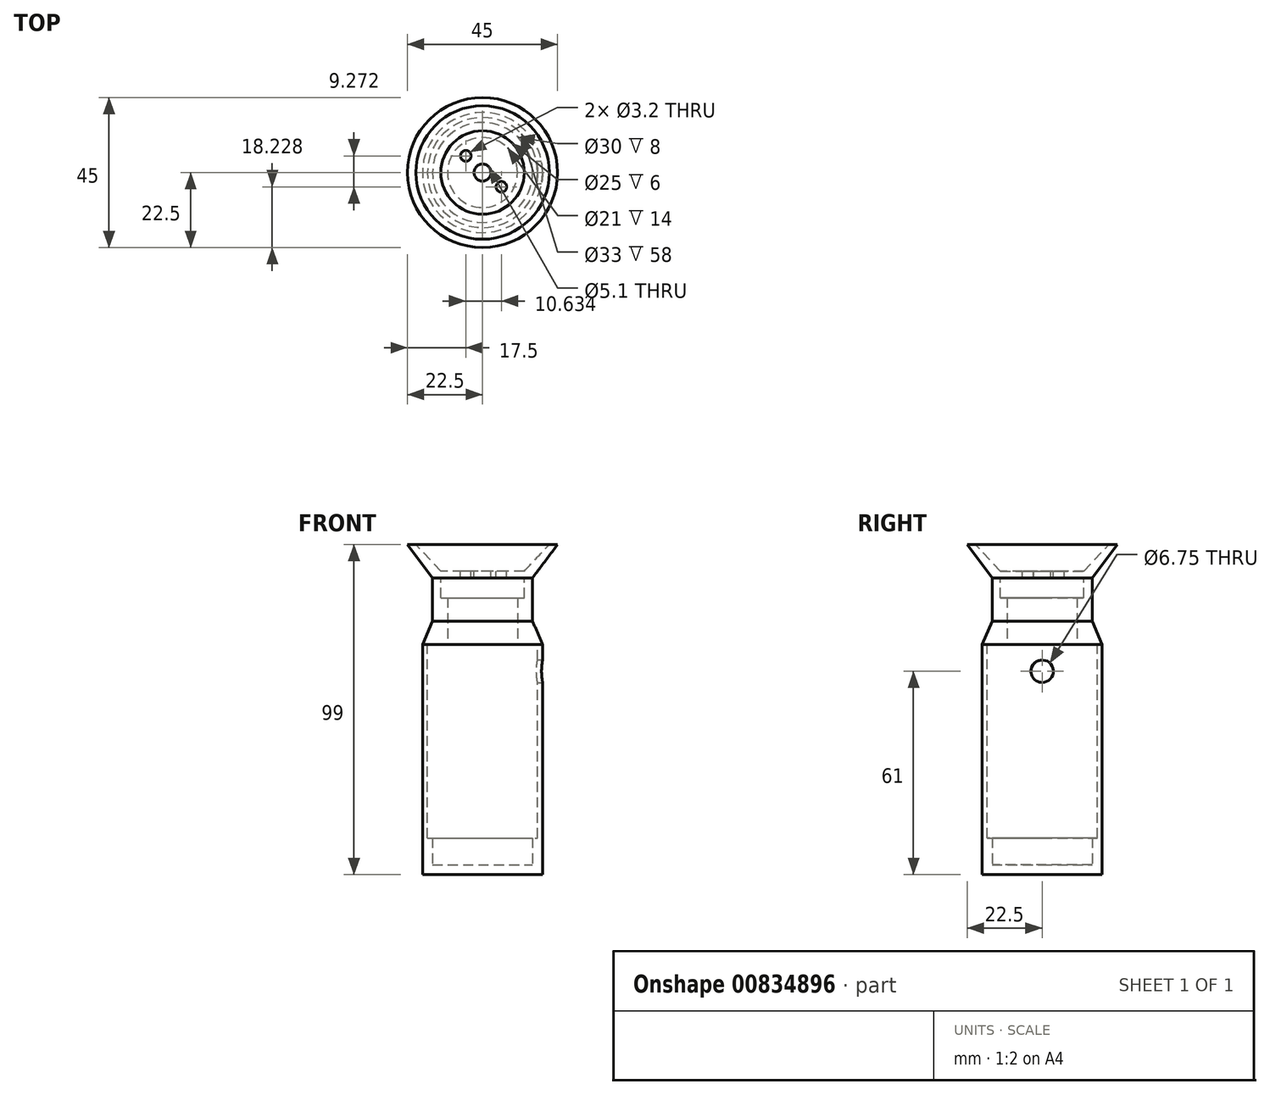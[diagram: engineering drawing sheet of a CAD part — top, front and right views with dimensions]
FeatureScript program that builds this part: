
annotation { "Feature Type Name" : "Feature", "Feature Type Description" : "" }
export const myFeature = defineFeature(function(context is Context, id is Id, definition is map)
    precondition{}
    {
        {
            var Q0;
            Q0=qCreatedBy(makeId("Top.planeOp"),FACE);
            var sketch = newSketch(context, id + "F0", { "sketchPlane" : qUnion([Q0])});
            skCircle(sketch, "E0", {"center": v(0, 0) * mm, "radius": 15 * mm});
            skSolve(sketch);
        }
        {
            var Q0;
            Q0=qCreatedBy(makeId("Top.planeOp"),FACE);
            cPlane(context, id + "F1", {"entities" : qUnion([Q0]), "cplaneType" : CPlaneType.OFFSET, "offset" : 10 * mm, "width" : 150 * mm, "height" : 150 * mm});
        }
        {
            var Q0;
            Q0=qCreatedBy(id+"F1.planeOp",FACE);
            var sketch = newSketch(context, id + "F2", { "sketchPlane" : qUnion([Q0])});
            skCircle(sketch, "E1", {"center": v(0, 0) * mm, "radius": 22.5 * mm});
            skSolve(sketch);
        }
        {
            var Q0;
            Q0 = qSketchRegion(id + "F2", true);
            var Q1;
            Q1 = qSketchRegion(id + "F0", true);
            loft(context, id + "F3", {"sheetProfilesArray" : [{ "sheetProfileEntities" : qUnion([Q0]) }, { "sheetProfileEntities" : qUnion([Q1]) }]});
        }
        {
            var Q0;
            Q0=makeQuery(id+"F3.opLoft","CAP_FACE",FACE,{"disambiguationData":[OSD([makeQuery(id+"F2.imprint","IMPRINT",FACE,{"disambiguationData":[TD([[makeQuery(id+"F2.imprint","IMPRINT",EDGE,{"derivedFrom":sQuery(id+"F2.wireOp",EDGE,"E1")}),1.0]])]})])],"isStart":true});
            var sketch = newSketch(context, id + "F4", { "sketchPlane" : qUnion([Q0])});
            skCircle(sketch, "E2", {"center": v(0, 0) * mm, "radius": 20 * mm});
            skSolve(sketch);
        }
        {
            var Q0;
            Q0=qCreatedBy(makeId("Top.planeOp"),FACE);
            cPlane(context, id + "F5", {"entities" : qUnion([Q0]), "cplaneType" : CPlaneType.OFFSET, "offset" : 2 * mm, "width" : 150 * mm, "height" : 150 * mm});
        }
        {
            var Q0;
            Q0=qCreatedBy(id+"F5.planeOp",FACE);
            var sketch = newSketch(context, id + "F6", { "sketchPlane" : qUnion([Q0])});
            skCircle(sketch, "E3", {"center": v(0, 0) * mm, "radius": 12.5 * mm});
            skSolve(sketch);
        }
        {
            var Q1;
            Q1 = qSketchRegion(id + "F6", true);
            var Q2;
            Q2 = qSketchRegion(id + "F4", true);
            loft(context, id + "F7", {"operationType" : NewBodyOperationType.REMOVE, "sheetProfilesArray" : [{ "sheetProfileEntities" : qUnion([Q1]) }, { "sheetProfileEntities" : qUnion([Q2]) }]});
        }
        {
            var Q0;
            Q0=makeQuery(id+"F3.opLoft","CAP_FACE",FACE,{"disambiguationData":[OSD([makeQuery(id+"F0.imprint","IMPRINT",FACE,{"disambiguationData":[TD([[makeQuery(id+"F0.imprint","IMPRINT",EDGE,{"derivedFrom":sQuery(id+"F0.wireOp",EDGE,"E0")}),1.0]])]})])],"isStart":true});
            var sketch = newSketch(context, id + "F8", { "sketchPlane" : qUnion([Q0])});
            skCircle(sketch, "E4", {"center": v(0, 0) * mm, "radius": 12.5 * mm});
            skSolve(sketch);
        }
        {
            var Q0;
            Q0=makeQuery(id+"F8.imprint","IMPRINT",FACE,{"disambiguationData":[TD([[makeQuery(id+"F8.imprint","IMPRINT",EDGE,{"derivedFrom":sQuery(id+"F8.wireOp",EDGE,"E4")}),-1.0]])]});
            extrude(context, id + "F9", {"entities" : qUnion([Q0]), "operationType" : NewBodyOperationType.ADD, "depth" : 13 * mm, "offsetDistance" : 25 * mm});
        }
        {
            var Q0;
            Q0=makeQuery(id+"F9.opExtrude","CAP_FACE",FACE,{"disambiguationData":[OSD([sQuery(id+"F8.wireOp",EDGE,"E4")])],"isStart":false});
            var sketch = newSketch(context, id + "F10", { "sketchPlane" : qUnion([Q0])});
            skCircle(sketch, "E5", {"center": v(0, 0) * mm, "radius": 10.5 * mm});
            skSolve(sketch);
        }
        {
            var Q0;
            Q0=makeQuery(id+"F10.imprint","IMPRINT",FACE,{"disambiguationData":[TD([[makeQuery(id+"F10.imprint","IMPRINT",EDGE,{"derivedFrom":sQuery(id+"F10.wireOp",EDGE,"E5")}),-1.0]])]});
            extrude(context, id + "F11", {"entities" : qUnion([Q0]), "oppositeDirection" : true, "depth" : 7 * mm, "offsetDistance" : 25 * mm});
        }
        {
            var Q0;
            Q0=makeQuery(id+"F9.opExtrude","CAP_FACE",FACE,{"disambiguationData":[OSD([sQuery(id+"F0.wireOp",EDGE,"E0"),sQuery(id+"F8.wireOp",EDGE,"E4")])],"isStart":false});
            var sketch = newSketch(context, id + "F12", { "sketchPlane" : qUnion([Q0])});
            skCircle(sketch, "E6.0", {"center": v(0, 0) * mm, "radius": 15 * mm});
            skSolve(sketch);
        }
        {
            var Q0;
            Q0=qCreatedBy(makeId("Top.planeOp"),FACE);
            cPlane(context, id + "F13", {"entities" : qUnion([Q0]), "cplaneType" : CPlaneType.OFFSET, "offset" : 20 * mm, "oppositeDirection" : true, "width" : 150 * mm, "height" : 150 * mm});
        }
        {
            var Q0;
            Q0=qCreatedBy(id+"F13.planeOp",FACE);
            var sketch = newSketch(context, id + "F14", { "sketchPlane" : qUnion([Q0])});
            skCircle(sketch, "E7", {"center": v(0, 0) * mm, "radius": 18 * mm});
            skSolve(sketch);
        }
        {
            var Q1;
            Q1 = qSketchRegion(id + "F12", true);
            var Q2;
            Q2 = qSketchRegion(id + "F14", true);
            loft(context, id + "F15", {"operationType" : NewBodyOperationType.ADD, "sheetProfilesArray" : [{ "sheetProfileEntities" : qUnion([Q1]) }, { "sheetProfileEntities" : qUnion([Q2]) }]});
        }
        {
            var Q0;
            Q0=makeQuery(id+"F15.opLoft","CAP_FACE",FACE,{"disambiguationData":[OSD([makeQuery(id+"F14.imprint","IMPRINT",FACE,{"disambiguationData":[TD([[makeQuery(id+"F14.imprint","IMPRINT",EDGE,{"derivedFrom":sQuery(id+"F14.wireOp",EDGE,"E7")}),1.0]])]})])],"isStart":true});
            var sketch = newSketch(context, id + "F16", { "sketchPlane" : qUnion([Q0])});
            skCircle(sketch, "E8", {"center": v(0, 0) * mm, "radius": 10.5 * mm});
            skSolve(sketch);
        }
        {
            var Q0;
            Q0=makeQuery(id+"F16.imprint","IMPRINT",FACE,{"disambiguationData":[TD([[makeQuery(id+"F16.imprint","IMPRINT",EDGE,{"derivedFrom":sQuery(id+"F16.wireOp",EDGE,"E8")}),1.0]])]});
            extrude(context, id + "F17", {"entities" : qUnion([Q0]), "operationType" : NewBodyOperationType.REMOVE, "oppositeDirection" : true, "depth" : 10 * mm, "offsetDistance" : 25 * mm});
        }
        {
            var Q0;
            Q0=makeQuery(id+"F15.opLoft","CAP_FACE",FACE,{"disambiguationData":[OSD([makeQuery(id+"F14.imprint","IMPRINT",FACE,{"disambiguationData":[TD([[makeQuery(id+"F14.imprint","IMPRINT",EDGE,{"derivedFrom":sQuery(id+"F14.wireOp",EDGE,"E7")}),1.0]])]})])],"isStart":true});
            var sketch = newSketch(context, id + "F18", { "sketchPlane" : qUnion([Q0])});
            skCircle(sketch, "E9", {"center": v(0, 0) * mm, "radius": 16.5 * mm});
            skSolve(sketch);
        }
        {
            var Q0;
            Q0=makeQuery(id+"F18.imprint","IMPRINT",FACE,{"disambiguationData":[TD([[makeQuery(id+"F18.imprint","IMPRINT",EDGE,{"derivedFrom":sQuery(id+"F18.wireOp",EDGE,"E9")}),-1.0]])]});
            extrude(context, id + "F19", {"entities" : qUnion([Q0]), "operationType" : NewBodyOperationType.ADD, "depth" : 62 * mm, "offsetDistance" : 25 * mm});
        }
        {
            var Q0;
            Q0=makeQuery(id+"F19.opExtrude","CAP_FACE",FACE,{"disambiguationData":[OSD([sQuery(id+"F14.wireOp",EDGE,"E7"),sQuery(id+"F18.wireOp",EDGE,"E9")])],"isStart":false});
            var sketch = newSketch(context, id + "F20", { "sketchPlane" : qUnion([Q0])});
            skCircle(sketch, "E10", {"center": v(0, 0) * mm, "radius": 15 * mm});
            skSolve(sketch);
        }
        {
            var Q0;
            Q0=makeQuery(id+"F20.imprint","IMPRINT",FACE,{"disambiguationData":[TD([[makeQuery(id+"F20.imprint","IMPRINT",EDGE,{"derivedFrom":sQuery(id+"F20.wireOp",EDGE,"E10")}),-1.0]])]});
            extrude(context, id + "F21", {"entities" : qUnion([Q0]), "oppositeDirection" : true, "depth" : 4 * mm, "offsetDistance" : 25 * mm});
        }
        {
            var Q0;
            Q0=makeQuery(id+"F21.opExtrude","CAP_FACE",FACE,{"disambiguationData":[OSD([sQuery(id+"F18.wireOp",EDGE,"E9"),sQuery(id+"F20.wireOp",EDGE,"E10")])],"isStart":true});
            var Q1;
            Q1=makeQuery(id+"F19.opExtrude","CAP_FACE",FACE,{"disambiguationData":[OSD([sQuery(id+"F14.wireOp",EDGE,"E7"),sQuery(id+"F18.wireOp",EDGE,"E9")])],"isStart":false});
            extrude(context, id + "F22", {"entities" : qUnion([Q0, Q1]), "operationType" : NewBodyOperationType.ADD, "depth" : 4 * mm, "offsetDistance" : 25 * mm});
        }
        {
            var Q0;
            {var subQ0=sQuery(id+"F18.wireOp",EDGE,"E9");Q0=makeQuery(id+"F22.boolean.opBoolean","MERGE",FACE,{"derivedFrom":[makeQuery(id+"F22.opExtrude","CAP_FACE",FACE,{"disambiguationData":[OSD([sQuery(id+"F14.wireOp",EDGE,"E7"),subQ0])],"isStart":false}),makeQuery(id+"F22.opExtrude","CAP_FACE",FACE,{"disambiguationData":[OSD([subQ0,sQuery(id+"F20.wireOp",EDGE,"E10")])],"isStart":false})]});}
            var sketch = newSketch(context, id + "F23", { "sketchPlane" : qUnion([Q0])});
            skCircle(sketch, "E11", {"center": v(0, 0) * mm, "radius": 18 * mm});
            skSolve(sketch);
        }
        {
            var Q0;
            Q0 = qSketchRegion(id + "F23", true);
            extrude(context, id + "F24", {"entities" : qUnion([Q0]), "operationType" : NewBodyOperationType.ADD, "depth" : 3 * mm, "offsetDistance" : 25 * mm});
        }
        {
            var Q0;
            Q0=makeQuery(id+"F7.boolean.opBoolean","COPY",FACE,{"derivedFrom":makeQuery(id+"F7.opLoft","CAP_FACE",FACE,{"disambiguationData":[OSD([makeQuery(id+"F6.imprint","IMPRINT",FACE,{"disambiguationData":[TD([[makeQuery(id+"F6.imprint","IMPRINT",EDGE,{"derivedFrom":sQuery(id+"F6.wireOp",EDGE,"E3")}),1.0]])]})])],"isStart":true})});
            var sketch = newSketch(context, id + "F25", { "sketchPlane" : qUnion([Q0])});
            skCircle(sketch, "E12", {"center": v(0, 0) * mm, "radius": 2.55 * mm});
            skCircle(sketch, "E13", {"center": v(-5, 5) * mm, "radius": 1.6 * mm});
            skCircle(sketch, "E14", {"center": v(5.63, -4.27) * mm, "radius": 1.6 * mm});
            skSolve(sketch);
        }
        {
            var Q0;
            Q0=makeQuery(id+"F25.imprint","IMPRINT",FACE,{"disambiguationData":[TD([[makeQuery(id+"F25.imprint","IMPRINT",EDGE,{"derivedFrom":sQuery(id+"F25.wireOp",EDGE,"E13")}),1.0]])]});
            var Q1;
            Q1=makeQuery(id+"F25.imprint","IMPRINT",FACE,{"disambiguationData":[TD([[makeQuery(id+"F25.imprint","IMPRINT",EDGE,{"derivedFrom":sQuery(id+"F25.wireOp",EDGE,"E12")}),1.0]])]});
            var Q2;
            Q2=makeQuery(id+"F25.imprint","IMPRINT",FACE,{"disambiguationData":[TD([[makeQuery(id+"F25.imprint","IMPRINT",EDGE,{"derivedFrom":sQuery(id+"F25.wireOp",EDGE,"E14")}),1.0]])]});
            extrude(context, id + "F26", {"entities" : qUnion([Q0, Q1, Q2]), "operationType" : NewBodyOperationType.REMOVE, "oppositeDirection" : true, "depth" : 3 * mm, "offsetDistance" : 25 * mm});
        }
        {
            var Q0;
            Q0=qCreatedBy(makeId("Right.planeOp"),FACE);
            cPlane(context, id + "F27", {"entities" : qUnion([Q0]), "cplaneType" : CPlaneType.OFFSET, "offset" : 18 * mm, "width" : 150 * mm, "height" : 150 * mm});
        }
        {
            var Q0;
            Q0=qCreatedBy(id+"F27.planeOp",FACE);
            var sketch = newSketch(context, id + "F28", { "sketchPlane" : qUnion([Q0])});
            skCircle(sketch, "E15", {"center": v(0, -28) * mm, "radius": 3.38 * mm});
            skSolve(sketch);
        }
        {
            var Q0;
            Q0=makeQuery(id+"F28.imprint","IMPRINT",FACE,{"disambiguationData":[TD([[makeQuery(id+"F28.imprint","IMPRINT",EDGE,{"derivedFrom":sQuery(id+"F28.wireOp",EDGE,"E15")}),1.0]])]});
            extrude(context, id + "F29", {"entities" : qUnion([Q0]), "operationType" : NewBodyOperationType.REMOVE, "oppositeDirection" : true, "depth" : 3 * mm, "offsetDistance" : 25 * mm});
        }
    });
